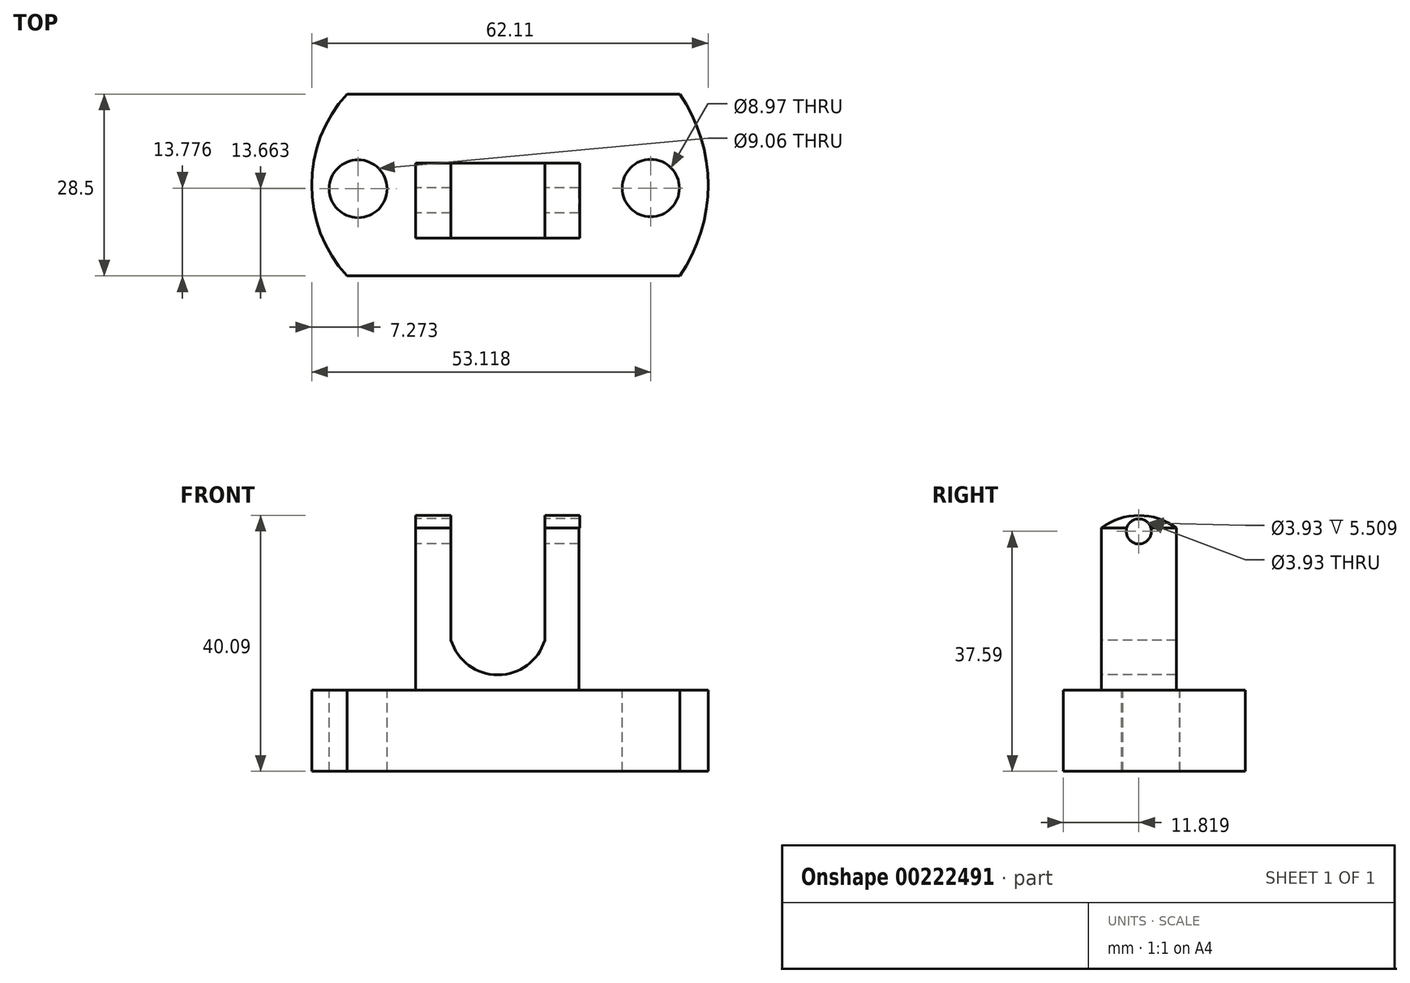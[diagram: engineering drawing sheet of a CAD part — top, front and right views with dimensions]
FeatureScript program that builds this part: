
annotation { "Feature Type Name" : "Feature", "Feature Type Description" : "" }
export const myFeature = defineFeature(function(context is Context, id is Id, definition is map)
    precondition{}
    {
        {
            var Q0;
            Q0=qCreatedBy(makeId("Top.planeOp"),FACE);
            var sketch = newSketch(context, id + "F0", { "sketchPlane" : qUnion([Q0])});
            skLineSegment(sketch, "E0.bottom", {"start": v(-36.35, 28.5) * mm, "end": v(15.76, 28.5) * mm});
            skLineSegment(sketch, "E0.top", {"start": v(-36.35, 0) * mm, "end": v(15.76, 0) * mm});
            skLineSegment(sketch, "E0.left", {"start": v(-36.35, 28.5) * mm, "end": v(-36.35, 0) * mm});
            skLineSegment(sketch, "E0.right", {"start": v(15.76, 28.5) * mm, "end": v(15.76, 0) * mm});
            skSolve(sketch);
        }
        {
            var Q0;
            Q0 = qSketchRegion(id + "F0", true);
            extrude(context, id + "F1", {"entities" : qUnion([Q0]), "depth" : 12.7 * mm});
        }
        {
            var Q0;
            Q0=makeQuery(id+"F1.opExtrude","CAP_FACE",FACE,{"disambiguationData":[OSD([sQuery(id+"F0.wireOp",EDGE,"E0.bottom"),sQuery(id+"F0.wireOp",EDGE,"E0.top"),sQuery(id+"F0.wireOp",EDGE,"E0.left"),sQuery(id+"F0.wireOp",EDGE,"E0.right")])],"isStart":false});
            var sketch = newSketch(context, id + "F2", { "sketchPlane" : qUnion([Q0])});
            skArc(sketch, "E1", {"start": v(-36.35, 28.5) * mm, "mid": v(-41.9, 14.25) * mm, "end": v(-36.35, 0) * mm});
            skSolve(sketch);
        }
        {
            var Q0;
            Q0=makeQuery(id+"F2.imprint","IMPRINT",FACE,{"disambiguationData":[TD([[makeQuery(id+"F2.imprint","IMPRINT",EDGE,{"derivedFrom":sQuery(id+"F2.wireOp",EDGE,"E1")}),1.0]])]});
            extrude(context, id + "F3", {"entities" : qUnion([Q0]), "operationType" : NewBodyOperationType.ADD, "oppositeDirection" : true, "depth" : 12.7 * mm});
        }
        {
            var Q0;
            {var subQ0=sQuery(id+"F0.wireOp",EDGE,"E0.left");Q0=makeQuery(id+"F3.boolean.opBoolean","MERGE",FACE,{"derivedFrom":[makeQuery(id+"F1.opExtrude","CAP_FACE",FACE,{"disambiguationData":[OSD([sQuery(id+"F0.wireOp",EDGE,"E0.bottom"),sQuery(id+"F0.wireOp",EDGE,"E0.top"),subQ0,sQuery(id+"F0.wireOp",EDGE,"E0.right")])],"isStart":false}),makeQuery(id+"F3.opExtrude","CAP_FACE",FACE,{"disambiguationData":[OSD([subQ0,sQuery(id+"F2.wireOp",EDGE,"E1")])],"isStart":true})]});}
            var sketch = newSketch(context, id + "F4", { "sketchPlane" : qUnion([Q0])});
            skArc(sketch, "E2", {"start": v(15.76, 0) * mm, "mid": v(20.22, 14.25) * mm, "end": v(15.76, 28.5) * mm});
            skSolve(sketch);
        }
        {
            var Q0;
            Q0=makeQuery(id+"F4.imprint","IMPRINT",FACE,{"disambiguationData":[TD([[makeQuery(id+"F4.imprint","IMPRINT",EDGE,{"derivedFrom":sQuery(id+"F4.wireOp",EDGE,"E2")}),1.0]])]});
            extrude(context, id + "F5", {"entities" : qUnion([Q0]), "operationType" : NewBodyOperationType.ADD, "oppositeDirection" : true, "depth" : 12.7 * mm});
        }
        {
            var Q0;
            {var subQ0=sQuery(id+"F0.wireOp",EDGE,"E0.right");var subQ1=sQuery(id+"F0.wireOp",EDGE,"E0.left");Q0=makeQuery(id+"F5.boolean.opBoolean","MERGE",FACE,{"derivedFrom":[makeQuery(id+"F3.boolean.opBoolean","MERGE",FACE,{"derivedFrom":[makeQuery(id+"F1.opExtrude","CAP_FACE",FACE,{"disambiguationData":[OSD([sQuery(id+"F0.wireOp",EDGE,"E0.bottom"),sQuery(id+"F0.wireOp",EDGE,"E0.top"),subQ1,subQ0])],"isStart":false}),makeQuery(id+"F3.opExtrude","CAP_FACE",FACE,{"disambiguationData":[OSD([subQ1,sQuery(id+"F2.wireOp",EDGE,"E1")])],"isStart":true})]}),makeQuery(id+"F5.opExtrude","CAP_FACE",FACE,{"disambiguationData":[OSD([subQ0,sQuery(id+"F4.wireOp",EDGE,"E2")])],"isStart":true})]});}
            var sketch = newSketch(context, id + "F6", { "sketchPlane" : qUnion([Q0])});
            skLineSegment(sketch, "E3.bottom", {"start": v(0, 17.7) * mm, "end": v(-25.64, 17.7) * mm});
            skLineSegment(sketch, "E3.top", {"start": v(0, 5.94) * mm, "end": v(-25.64, 5.94) * mm});
            skLineSegment(sketch, "E3.left", {"start": v(0, 17.7) * mm, "end": v(0, 5.94) * mm});
            skLineSegment(sketch, "E3.right", {"start": v(-25.64, 17.7) * mm, "end": v(-25.64, 5.94) * mm});
            skSolve(sketch);
        }
        {
            var Q0;
            Q0 = qSketchRegion(id + "F6", true);
            extrude(context, id + "F7", {"entities" : qUnion([Q0]), "operationType" : NewBodyOperationType.ADD, "depth" : 25.4 * mm});
        }
        {
            var Q0;
            Q0=makeQuery(id+"F7.opExtrude","SWEPT_FACE",FACE,{"disambiguationData":[OSD([sQuery(id+"F6.wireOp",EDGE,"E3.right")])]});
            var sketch = newSketch(context, id + "F8", { "sketchPlane" : qUnion([Q0])});
            skArc(sketch, "E4", {"start": v(-5.94, 38.1) * mm, "mid": v(-11.82, 40.09) * mm, "end": v(-17.7, 38.1) * mm});
            skSolve(sketch);
        }
        {
            var Q0;
            Q0=makeQuery(id+"F8.imprint","IMPRINT",FACE,{"disambiguationData":[TD([[makeQuery(id+"F8.imprint","IMPRINT",EDGE,{"derivedFrom":sQuery(id+"F8.wireOp",EDGE,"E4")}),1.0]])]});
            extrude(context, id + "F9", {"entities" : qUnion([Q0]), "operationType" : NewBodyOperationType.ADD, "oppositeDirection" : true, "depth" : 25.78 * mm});
        }
        {
            var Q0;
            Q0=makeQuery(id+"F7.opExtrude","SWEPT_FACE",FACE,{"disambiguationData":[OSD([sQuery(id+"F6.wireOp",EDGE,"E3.top")])]});
            var sketch = newSketch(context, id + "F10", { "sketchPlane" : qUnion([Q0])});
            skLineSegment(sketch, "E5", {"start": v(-20.06, 40.26) * mm, "end": v(-20.06, 20.54) * mm});
            skLineSegment(sketch, "E6", {"start": v(-20.06, 20.54) * mm, "end": v(-5.37, 20.54) * mm});
            skLineSegment(sketch, "E7", {"start": v(-5.37, 20.54) * mm, "end": v(-5.37, 40.5) * mm});
            skLineSegment(sketch, "E8", {"start": v(-5.37, 40.5) * mm, "end": v(-20.06, 40.26) * mm});
            skSolve(sketch);
        }
        {
            var Q0;
            {var subQ0=sQuery(id+"F10.wireOp",EDGE,"E8");Q0=makeQuery(id+"F10.imprint","IMPRINT",FACE,{"disambiguationData":[TD([[makeQuery(id+"F10.imprint","IMPRINT",EDGE,{"derivedFrom":subQ0}),1.0]])]});}
            var Q1;
            {var subQ0=sQuery(id+"F10.wireOp",EDGE,"E6");Q1=makeQuery(id+"F10.imprint","IMPRINT",FACE,{"disambiguationData":[TD([[makeQuery(id+"F10.imprint","IMPRINT",EDGE,{"derivedFrom":subQ0}),1.0]])]});}
            extrude(context, id + "F11", {"entities" : qUnion([Q0, Q1]), "operationType" : NewBodyOperationType.REMOVE, "endBound" : BoundingType.THROUGH_ALL, "oppositeDirection" : true, "depth" : 25.4 * mm});
        }
        {
            var Q0;
            {var subQ0=sQuery(id+"F0.wireOp",EDGE,"E0.right");var subQ1=sQuery(id+"F0.wireOp",EDGE,"E0.left");Q0=makeQuery(id+"F5.boolean.opBoolean","MERGE",FACE,{"derivedFrom":[makeQuery(id+"F3.boolean.opBoolean","MERGE",FACE,{"derivedFrom":[makeQuery(id+"F1.opExtrude","CAP_FACE",FACE,{"disambiguationData":[OSD([sQuery(id+"F0.wireOp",EDGE,"E0.bottom"),sQuery(id+"F0.wireOp",EDGE,"E0.top"),subQ1,subQ0])],"isStart":false}),makeQuery(id+"F3.opExtrude","CAP_FACE",FACE,{"disambiguationData":[OSD([subQ1,sQuery(id+"F2.wireOp",EDGE,"E1")])],"isStart":true})]}),makeQuery(id+"F5.opExtrude","CAP_FACE",FACE,{"disambiguationData":[OSD([subQ0,sQuery(id+"F4.wireOp",EDGE,"E2")])],"isStart":true})]});}
            var sketch = newSketch(context, id + "F12", { "sketchPlane" : qUnion([Q0])});
            skCircle(sketch, "E9", {"center": v(-34.62, 13.66) * mm, "radius": 4.53 * mm});
            skCircle(sketch, "E10", {"center": v(11.23, 13.78) * mm, "radius": 4.49 * mm});
            skSolve(sketch);
        }
        {
            var Q0;
            Q0=makeQuery(id+"F12.imprint","IMPRINT",FACE,{"disambiguationData":[TD([[makeQuery(id+"F12.imprint","IMPRINT",EDGE,{"derivedFrom":sQuery(id+"F12.wireOp",EDGE,"E9")}),1.0]])]});
            var Q1;
            Q1=makeQuery(id+"F12.imprint","IMPRINT",FACE,{"disambiguationData":[TD([[makeQuery(id+"F12.imprint","IMPRINT",EDGE,{"derivedFrom":sQuery(id+"F12.wireOp",EDGE,"E10")}),1.0]])]});
            extrude(context, id + "F13", {"entities" : qUnion([Q0, Q1]), "operationType" : NewBodyOperationType.REMOVE, "endBound" : BoundingType.THROUGH_ALL, "oppositeDirection" : true, "depth" : 25.4 * mm});
        }
        {
            var Q0;
            {var subQ0=sQuery(id+"F6.wireOp",EDGE,"E3.right");Q0=makeQuery(id+"F9.boolean.opBoolean","MERGE",FACE,{"derivedFrom":[makeQuery(id+"F7.opExtrude","SWEPT_FACE",FACE,{"disambiguationData":[OSD([subQ0])]}),makeQuery(id+"F9.opExtrude","CAP_FACE",FACE,{"disambiguationData":[OSD([subQ0,sQuery(id+"F8.wireOp",EDGE,"E4")])],"isStart":true})]});}
            var sketch = newSketch(context, id + "F14", { "sketchPlane" : qUnion([Q0])});
            skCircle(sketch, "E11", {"center": v(-11.82, 37.59) * mm, "radius": 1.97 * mm});
            skPoint(sketch, "E11.centerSnap0", {"position": v(-11.82, 40.09) * mm});
            skSolve(sketch);
        }
        {
            var Q0;
            Q0 = qSketchRegion(id + "F14", true);
            extrude(context, id + "F15", {"entities" : qUnion([Q0]), "operationType" : NewBodyOperationType.REMOVE, "endBound" : BoundingType.THROUGH_ALL, "oppositeDirection" : true, "depth" : 25.4 * mm});
        }
        {
            var Q0;
            Q0=makeQuery(id+"F7.opExtrude","SWEPT_FACE",FACE,{"disambiguationData":[OSD([sQuery(id+"F6.wireOp",EDGE,"E3.top")])]});
            var sketch = newSketch(context, id + "F16", { "sketchPlane" : qUnion([Q0])});
            skArc(sketch, "E12", {"start": v(-20.06, 20.54) * mm, "mid": v(-12.72, 15.1) * mm, "end": v(-5.37, 20.54) * mm});
            skLineSegment(sketch, "E13", {"start": v(-20.06, 20.54) * mm, "end": v(-5.37, 20.54) * mm});
            skSolve(sketch);
        }
        {
            var Q0;
            Q0 = qSketchRegion(id + "F16", true);
            extrude(context, id + "F17", {"entities" : qUnion([Q0]), "operationType" : NewBodyOperationType.REMOVE, "endBound" : BoundingType.THROUGH_ALL, "oppositeDirection" : true, "depth" : 25.4 * mm});
        }
    });
